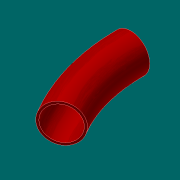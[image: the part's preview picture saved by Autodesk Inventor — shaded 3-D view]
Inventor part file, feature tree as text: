
AUTODESK INVENTOR PART (.ipt)
format: ipt  version: 2017.3 (Build 213257000, 257)  size: 143,872 bytes
history: native  units: in
note: dims shown in document units (in); Inventor stores cm internally (conversion verified against a paired STEP export)
features: other x3, revolve x1, sketch x1
ambient origin geometry x8: Origin, YZ Plane, XZ Plane, XY Plane, X Axis, Y Axis, Z Axis, Center Point
bodies: Solid1 (feature_tree)
feature tree (5):
  other  "A1-19027-100-05 HCWI elbow - female.ipt"
  revolve  "Revolution1"  [1 undecoded]
  other  "Solid1::A1-19027-100-05 HCWI elbow - female.ipt"
  other  "TaggingFeature1"
  sketch  "Sketch1"  dims[d0=0.3937in d1=0.213in]
note: 1 required parameter value undecoded (feature->parameter linkage not recoverable at this tier; creation-order binding heuristic only, values carry confidence <= 0.55)
